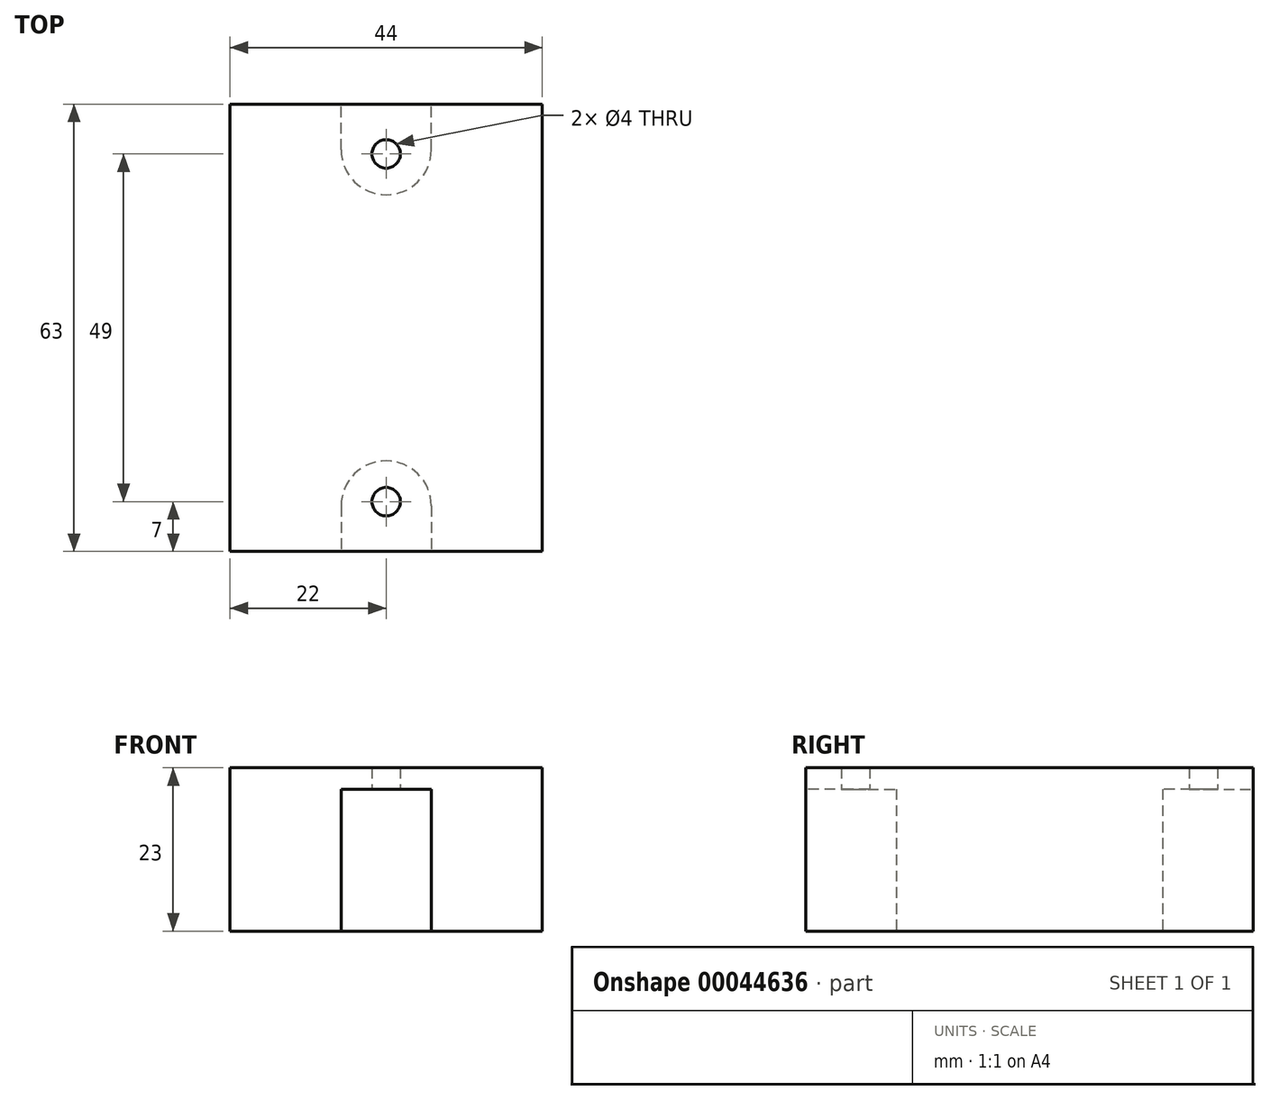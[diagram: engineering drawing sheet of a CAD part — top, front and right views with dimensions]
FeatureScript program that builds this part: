
annotation { "Feature Type Name" : "Feature", "Feature Type Description" : "" }
export const myFeature = defineFeature(function(context is Context, id is Id, definition is map)
    precondition{}
    {
        {
            var Q0;
            Q0=qCreatedBy(makeId("Top.planeOp"),FACE);
            var sketch = newSketch(context, id + "F0", { "sketchPlane" : qUnion([Q0])});
            skLineSegment(sketch, "E0.rect.bottom", {"start": v(22, 31.5) * mm, "end": v(-22, 31.5) * mm});
            skLineSegment(sketch, "E0.rect.top", {"start": v(22, -31.5) * mm, "end": v(-22, -31.5) * mm});
            skLineSegment(sketch, "E0.rect.left", {"start": v(22, 31.5) * mm, "end": v(22, -31.5) * mm});
            skLineSegment(sketch, "E0.rect.right", {"start": v(-22, 31.5) * mm, "end": v(-22, -31.5) * mm});
            skPoint(sketch, "E0.rect.middle", {"position": v(0, 0) * mm});
            skCircle(sketch, "E1", {"center": v(0, 24.5) * mm, "radius": 2 * mm});
            skCircle(sketch, "E2.MirrorC", {"center": v(0, -24.5) * mm, "radius": 2 * mm});
            skSolve(sketch);
        }
        {
            var Q0;
            Q0=makeQuery(id+"F0.imprint","IMPRINT",FACE,{"disambiguationData":[TD([[makeQuery(id+"F0.imprint","IMPRINT",EDGE,{"derivedFrom":sQuery(id+"F0.wireOp",EDGE,"E0.rect.bottom")}),1.0]])]});
            extrude(context, id + "F1", {"entities" : qUnion([Q0]), "depth" : 23 * mm});
        }
        {
            var Q0;
            Q0=qCreatedBy(makeId("Top.planeOp"),FACE);
            var sketch = newSketch(context, id + "F2", { "sketchPlane" : qUnion([Q0])});
            skArc(sketch, "E3", {"start": v(0, 18.74) * mm, "mid": v(4.49, 20.6) * mm, "end": v(6.35, 25.08) * mm});
            skLineSegment(sketch, "E4", {"start": v(6.35, 25.08) * mm, "end": v(6.36, 31.54) * mm});
            skLineSegment(sketch, "E5", {"start": v(6.36, 31.54) * mm, "end": v(0, 31.55) * mm});
            skLineSegment(sketch, "E6.MirrorCS", {"start": v(-6.35, 25.08) * mm, "end": v(-6.36, 31.54) * mm});
            skLineSegment(sketch, "E7.MirrorCS", {"start": v(-6.36, 31.54) * mm, "end": v(0, 31.55) * mm});
            skArc(sketch, "E8.MirrorCS", {"start": v(0, 18.74) * mm, "mid": v(-4.49, 20.6) * mm, "end": v(-6.35, 25.08) * mm});
            skArc(sketch, "E9.MirrorCS", {"start": v(0, -18.74) * mm, "mid": v(4.49, -20.6) * mm, "end": v(6.35, -25.08) * mm});
            skArc(sketch, "E10.MirrorCS", {"start": v(0, -18.74) * mm, "mid": v(-4.49, -20.6) * mm, "end": v(-6.35, -25.08) * mm});
            skLineSegment(sketch, "E11.MirrorCS", {"start": v(-6.35, -25.08) * mm, "end": v(-6.36, -31.54) * mm});
            skLineSegment(sketch, "E12.MirrorCS", {"start": v(-6.36, -31.54) * mm, "end": v(0, -31.55) * mm});
            skLineSegment(sketch, "E13.MirrorCS", {"start": v(6.35, -25.08) * mm, "end": v(6.36, -31.54) * mm});
            skLineSegment(sketch, "E14.MirrorCS", {"start": v(6.36, -31.54) * mm, "end": v(0, -31.55) * mm});
            skSolve(sketch);
        }
        {
            var Q0;
            Q0=qSketchRegion(id+"F2",true);
            extrude(context, id + "F3", {"entities" : qUnion([Q0]), "operationType" : NewBodyOperationType.REMOVE, "depth" : 20 * mm});
        }
    });
